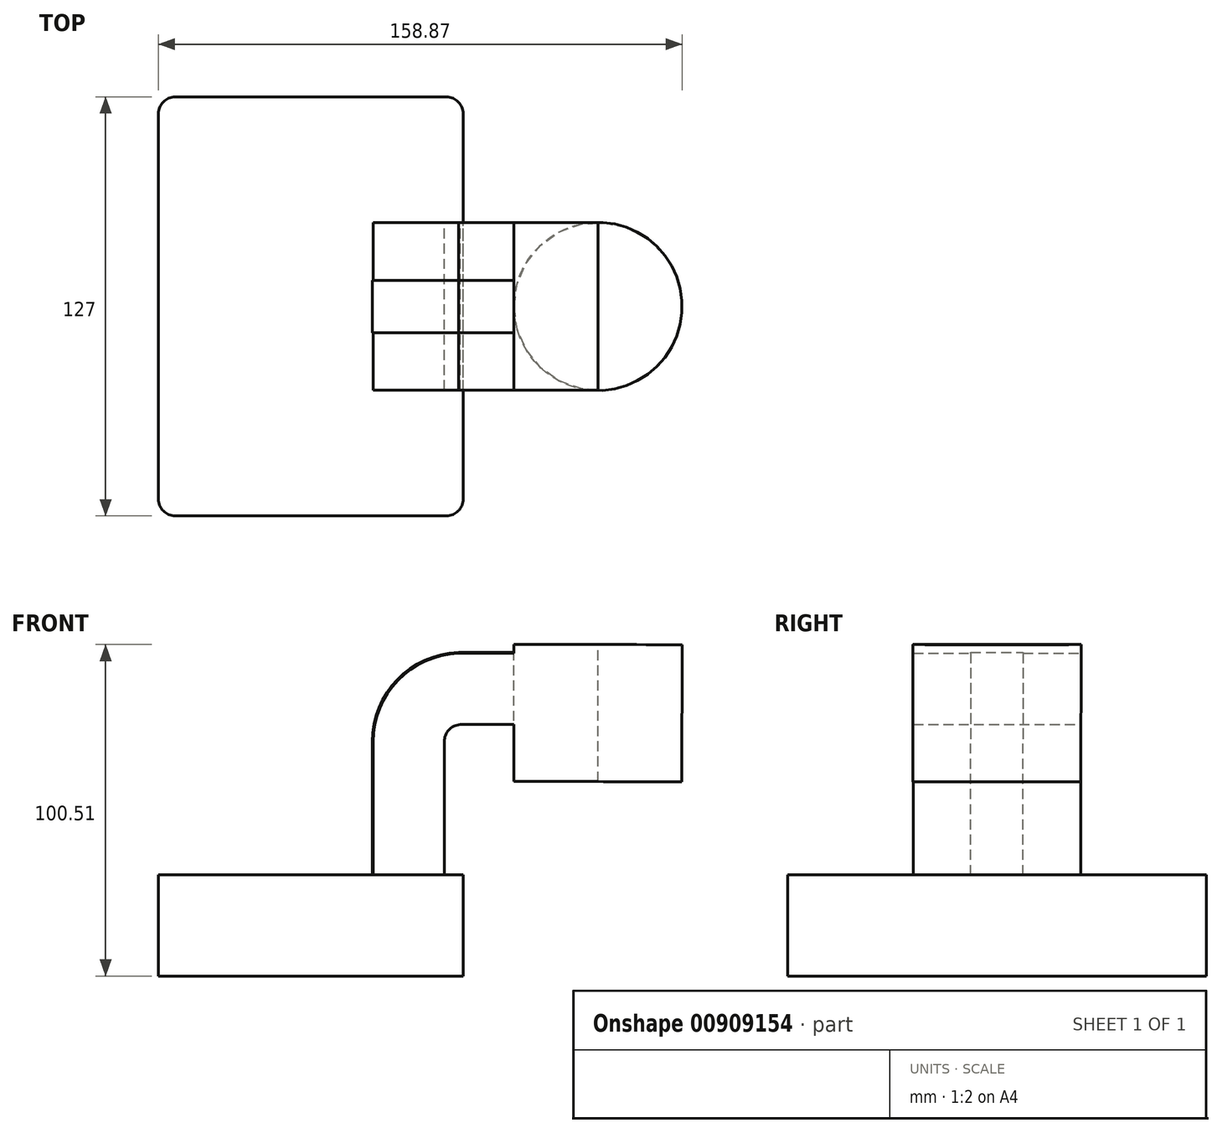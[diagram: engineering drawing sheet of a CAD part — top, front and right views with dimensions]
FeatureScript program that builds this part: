
annotation { "Feature Type Name" : "Feature", "Feature Type Description" : "" }
export const myFeature = defineFeature(function(context is Context, id is Id, definition is map)
    precondition{}
    {
        {
            var Q0;
            Q0=qCreatedBy(makeId("Front.planeOp"),FACE);
            var sketch = newSketch(context, id + "F0", { "sketchPlane" : qUnion([Q0])});
            skLineSegment(sketch, "E0.bottom", {"start": v(-42.46, -15.33) * mm, "end": v(50, -15.33) * mm});
            skLineSegment(sketch, "E0.top", {"start": v(-42.46, 15.33) * mm, "end": v(50, 15.33) * mm});
            skLineSegment(sketch, "E0.left", {"start": v(-42.46, -15.33) * mm, "end": v(-42.46, 15.33) * mm});
            skLineSegment(sketch, "E0.right", {"start": v(50, -15.33) * mm, "end": v(50, 15.33) * mm});
            skLineSegment(sketch, "E1.bottom", {"start": v(116.33, 43.64) * mm, "end": v(65.41, 43.64) * mm});
            skLineSegment(sketch, "E1.top", {"start": v(116.33, 85.18) * mm, "end": v(65.41, 85.18) * mm});
            skLineSegment(sketch, "E1.left", {"start": v(116.33, 43.64) * mm, "end": v(116.33, 85.18) * mm});
            skLineSegment(sketch, "E1.right", {"start": v(65.41, 43.64) * mm, "end": v(65.41, 85.18) * mm});
            skPoint(sketch, "E1.middle", {"position": v(90.87, 64.4) * mm});
            skLineSegment(sketch, "E2", {"start": v(33.59, 15.33) * mm, "end": v(33.59, 55.7) * mm});
            skArc(sketch, "E3", {"start": v(33.59, 55.7) * mm, "mid": v(38, 66.68) * mm, "end": v(48.77, 71.56) * mm});
            skLineSegment(sketch, "E4", {"start": v(48.77, 71.56) * mm, "end": v(65.41, 71.56) * mm});
            skLineSegment(sketch, "E5.0", {"start": v(48.57, 82.48) * mm, "end": v(65.41, 82.48) * mm});
            skArc(sketch, "E5.1", {"start": v(22.66, 55.7) * mm, "mid": v(30.2, 74.33) * mm, "end": v(48.57, 82.48) * mm});
            skLineSegment(sketch, "E5.2", {"start": v(22.66, 15.33) * mm, "end": v(22.66, 55.7) * mm});
            skLineSegment(sketch, "E6.0", {"start": v(49.07, 60.89) * mm, "end": v(65.41, 60.89) * mm});
            skArc(sketch, "E6.1", {"start": v(44.25, 55.7) * mm, "mid": v(45.64, 59.24) * mm, "end": v(49.07, 60.89) * mm});
            skLineSegment(sketch, "E6.2", {"start": v(44.25, 15.33) * mm, "end": v(44.25, 55.7) * mm});
            skLineSegment(sketch, "E7.0", {"start": v(48.56, 82.74) * mm, "end": v(65.41, 82.74) * mm});
            skArc(sketch, "E7.1", {"start": v(22.4, 55.7) * mm, "mid": v(30.01, 74.5) * mm, "end": v(48.56, 82.74) * mm});
            skLineSegment(sketch, "E7.2", {"start": v(22.4, 15.33) * mm, "end": v(22.4, 55.7) * mm});
            skLineSegment(sketch, "E8", {"start": v(65.41, 71.56) * mm, "end": v(90.87, 71.53) * mm});
            skPoint(sketch, "E8.endSnap0", {"position": v(90.87, 43.64) * mm});
            skLineSegment(sketch, "E9", {"start": v(65.41, 82.74) * mm, "end": v(90.87, 82.74) * mm});
            skLineSegment(sketch, "E10", {"start": v(65.41, 60.89) * mm, "end": v(90.87, 60.86) * mm});
            skLineSegment(sketch, "E11", {"start": v(90.87, 43.64) * mm, "end": v(90.91, 85.18) * mm});
            skFitSpline(sketch, "E12", {"points": [v(-42.46, 15.33) * mm, v(48.56, 82.74) * mm], "startDerivative": vector(105.43, 203.6) * mm, "endDerivative": vector(66.33, -1.36) * mm});
            skSolve(sketch);
        }
        {
            var Q0;
            Q0=makeQuery(id+"F0.imprint","IMPRINT",FACE,{"disambiguationData":[TD([[makeQuery(id+"F0.imprint","IMPRINT",EDGE,{"derivedFrom":sQuery(id+"F0.wireOp",EDGE,"E0.bottom")}),1.0]])]});
            extrude(context, id + "F1", {"entities" : qUnion([Q0]), "endBound" : BoundingType.SYMMETRIC, "depth" : 127 * mm, "offsetDistance" : 25.4 * mm});
        }
        {
            var Q0;
            {var subQ0=sQuery(id+"F0.wireOp",EDGE,"E2");Q0=makeQuery(id+"F0.imprint","IMPRINT",FACE,{"disambiguationData":[TD([[makeQuery(id+"F0.imprint","IMPRINT",EDGE,{"derivedFrom":subQ0}),-1.0]])]});}
            var Q1;
            {var subQ3=sQuery(id+"F0.wireOp",EDGE,"E2");Q1=makeQuery(id+"F0.imprint","IMPRINT",FACE,{"disambiguationData":[TD([[makeQuery(id+"F0.imprint","IMPRINT",EDGE,{"derivedFrom":subQ3}),1.0]])]});}
            var Q2;
            {var subQ6=sQuery(id+"F0.wireOp",EDGE,"E11");Q2=makeQuery(id+"F0.imprint","IMPRINT",FACE,{"disambiguationData":[TD([[makeQuery(id+"F0.imprint","IMPRINT",EDGE,{"derivedFrom":subQ6}),1.0]])]});}
            extrude(context, id + "F2", {"entities" : qUnion([Q0, Q1, Q2]), "endBound" : BoundingType.SYMMETRIC, "depth" : 50.8 * mm, "offsetDistance" : 25.4 * mm});
        }
        {
            var Q0;
            Q0=makeQuery(id+"F0.imprint","IMPRINT",FACE,{"disambiguationData":[TD([[makeQuery(id+"F0.imprint","IMPRINT",EDGE,{"derivedFrom":sQuery(id+"F0.wireOp",EDGE,"E7.1")}),1.0]])]});
            extrude(context, id + "F3", {"entities" : qUnion([Q0]), "operationType" : NewBodyOperationType.ADD, "endBound" : BoundingType.SYMMETRIC, "depth" : 15.88 * mm, "offsetDistance" : 25.4 * mm});
        }
        {
            var Q0;
            {var subQ6=sQuery(id+"F0.wireOp",EDGE,"E11");Q0=makeQuery(id+"F0.imprint","IMPRINT",FACE,{"disambiguationData":[TD([[makeQuery(id+"F0.imprint","IMPRINT",EDGE,{"derivedFrom":subQ6}),1.0]])]});}
            var Q1;
            Q1=sQuery(id+"F0.wireOp",EDGE,"E11");
            revolve(context, id + "F4", {"surfaceOperationType" : NewSurfaceOperationType.NEW, "entities" : qUnion([Q0]), "axis" : qUnion([Q1]), "revolveType" : RevolveType.FULL});
        }
        {
            var Q0;
            Q0=makeQuery(id+"F1.opExtrude","CAP_EDGE",EDGE,{"disambiguationData":[OSD([sQuery(id+"F0.wireOp",EDGE,"E0.left")])],"isStart":false});
            var Q1;
            Q1=makeQuery(id+"F1.opExtrude","CAP_EDGE",EDGE,{"disambiguationData":[OSD([sQuery(id+"F0.wireOp",EDGE,"E0.right")])],"isStart":false});
            var Q2;
            Q2=makeQuery(id+"F1.opExtrude","CAP_EDGE",EDGE,{"disambiguationData":[OSD([sQuery(id+"F0.wireOp",EDGE,"E0.right")])],"isStart":true});
            var Q3;
            Q3=makeQuery(id+"F1.opExtrude","CAP_EDGE",EDGE,{"disambiguationData":[OSD([sQuery(id+"F0.wireOp",EDGE,"E0.left")])],"isStart":true});
            fillet(context, id + "F5", {"entities" : qUnion([Q0, Q1, Q2, Q3]), "radius" : 5.08 * mm, "tangentPropagation" : true, "allowEdgeOverflow" : false});
        }
    });
